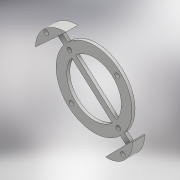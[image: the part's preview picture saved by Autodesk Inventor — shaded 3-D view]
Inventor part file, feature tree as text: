
AUTODESK INVENTOR PART (.ipt)
format: ipt  version: 2017 (Build 210142000, 142)  size: 183,296 bytes
history: native  units: mm
features: extrude x4, sketch x4
ambient origin geometry x8: Origin, YZ Plane, XZ Plane, XY Plane, X Axis, Y Axis, Z Axis, Center Point
bodies: Solid1 (feature_tree)
feature tree (8):
  extrude  "Extrusion1"  Depth=2.0mm
  extrude  "Extrusion2"  Depth=4.0mm
  extrude  "Extrusion3"  Depth=2.0mm
  extrude  "Extrusion4"  Depth=2.0mm
  sketch  "Sketch1"  dims[d0=8.0mm d1=0.0mm d2=2.0mm]
  sketch  "Sketch2"  dims[d3=4.0mm d4=4.0mm]
  sketch  "Sketch3"  dims[d5=2.0mm d6=0.0mm d9=3.0mm]
  sketch  "Sketch4"  dims[d10=3.0mm d11=3.0mm d12=3.0mm d13=2.0mm d14=0.0mm d15=3.0mm d16=3.0mm d17=3.0mm d18=3.0mm d19=2.0mm d20=0.0mm]
